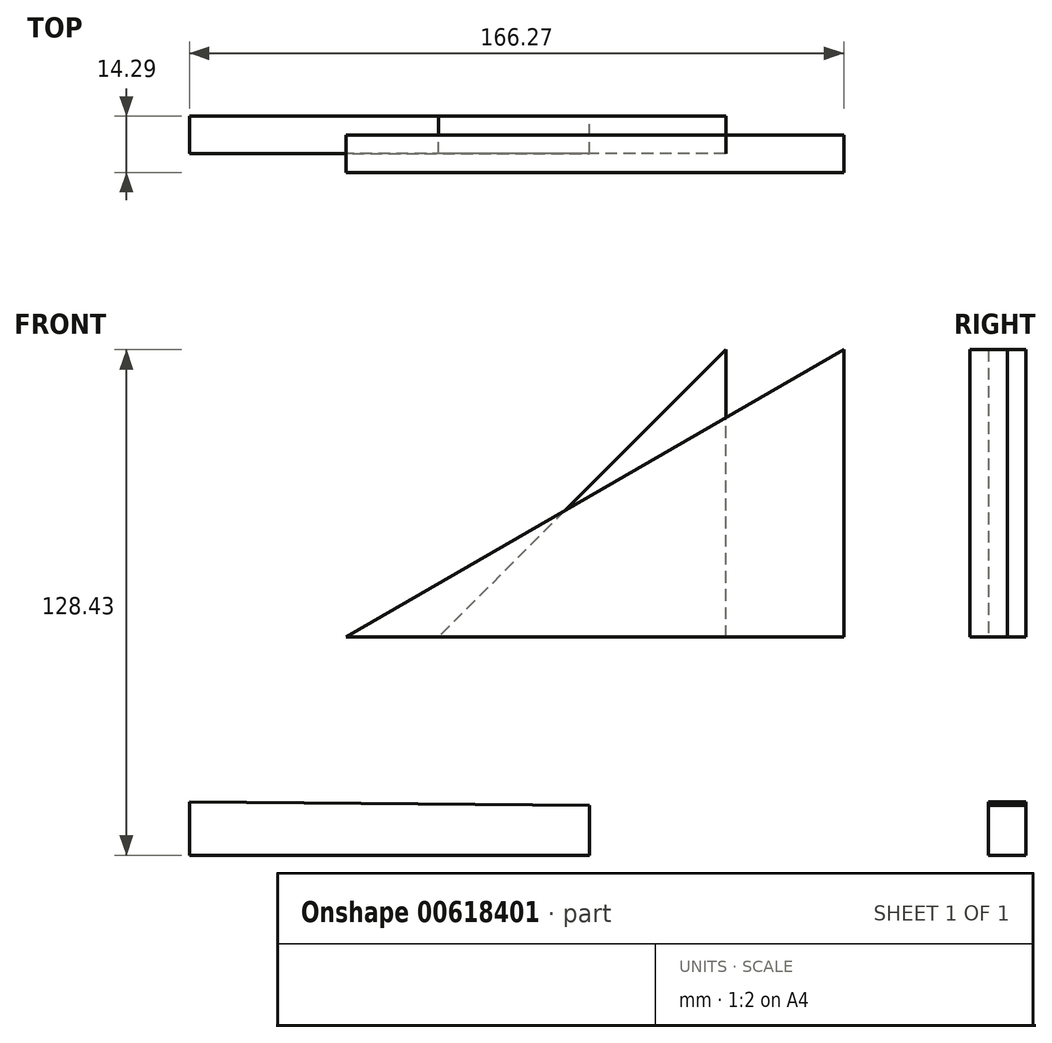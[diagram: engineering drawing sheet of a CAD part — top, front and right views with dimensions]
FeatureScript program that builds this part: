
annotation { "Feature Type Name" : "Feature", "Feature Type Description" : "" }
export const myFeature = defineFeature(function(context is Context, id is Id, definition is map)
    precondition{}
    {
        {
            var Q0;
            Q0=qCreatedBy(makeId("Front.planeOp"),FACE);
            var sketch = newSketch(context, id + "F0", { "sketchPlane" : qUnion([Q0])});
            skLineSegment(sketch, "E0", {"start": v(-59.68, 0) * mm, "end": v(66.8, 0) * mm});
            skLineSegment(sketch, "E1", {"start": v(66.8, 0) * mm, "end": v(66.8, 73.03) * mm});
            skLineSegment(sketch, "E2", {"start": v(66.8, 73.03) * mm, "end": v(-59.68, 0) * mm});
            skSolve(sketch);
        }
        {
            var Q0;
            Q0 = qSketchRegion(id + "F0", true);
            extrude(context, id + "F1", {"entities" : qUnion([Q0]), "depth" : 9.52 * mm, "offsetDistance" : 25.4 * mm});
        }
        {
            var Q0;
            Q0=qCreatedBy(makeId("Front.planeOp"),FACE);
            var sketch = newSketch(context, id + "F2", { "sketchPlane" : qUnion([Q0])});
            skLineSegment(sketch, "E3", {"start": v(-36.2, 0) * mm, "end": v(36.83, 0) * mm});
            skLineSegment(sketch, "E4", {"start": v(36.83, 0) * mm, "end": v(36.83, 73.03) * mm});
            skLineSegment(sketch, "E5", {"start": v(36.83, 73.03) * mm, "end": v(-36.2, 0) * mm});
            skLineSegment(sketch, "E6", {"start": v(-99.46, -55.4) * mm, "end": v(2.14, -55.4) * mm});
            skLineSegment(sketch, "E7", {"start": v(2.14, -55.4) * mm, "end": v(2.14, -42.7) * mm});
            skLineSegment(sketch, "E8", {"start": v(2.14, -42.7) * mm, "end": v(-99.46, -41.81) * mm});
            skLineSegment(sketch, "E9", {"start": v(-99.46, -55.4) * mm, "end": v(-99.46, -41.81) * mm});
            skSolve(sketch);
        }
        {
            var Q0;
            Q0 = qSketchRegion(id + "F2", true);
            extrude(context, id + "F3", {"entities" : qUnion([Q0]), "endBound" : BoundingType.SYMMETRIC, "depth" : 9.52 * mm, "offsetDistance" : 25.4 * mm});
        }
    });
